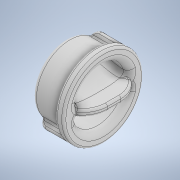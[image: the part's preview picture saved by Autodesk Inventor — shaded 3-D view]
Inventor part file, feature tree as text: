
AUTODESK INVENTOR PART (.ipt)
format: ipt  version: 2020 (Build 240168000, 168)  size: 1,119,744 bytes
history: native  units: in
note: dims shown in document units (in); Inventor stores cm internally (conversion verified against a paired STEP export)
features: fillet x10, extrude x5, sketch x5
ambient origin geometry x8: Origin, YZ Plane, XZ Plane, XY Plane, X Axis, Y Axis, Z Axis, Center Point
bodies: Solid1 (feature_tree)
feature tree (20):
  extrude  "Extrusion1"  Depth=0.5512in TaperAngle=0.0deg
  extrude  "Extrusion2"  TaperAngle=45.0deg  [1 undecoded]
  extrude  "Extrusion3"  Depth=0.0984in
  extrude  "Extrusion4"  Depth=0.4724in TaperAngle=0.0deg
  extrude  "Extrusion5"  Depth=0.1575in TaperAngle=0.0deg
  fillet  "Fillet1"  Radius=1.0236in
  fillet  "Fillet2"  Radius=0.5906in
  fillet  "Fillet3"  Radius=0.0591in
  fillet  "Fillet4"  Radius=0.0591in
  fillet  "Fillet5"  Radius=0.7874in
  fillet  "Fillet6"  Radius=0.5118in
  fillet  "Fillet7"  Radius=0.0787in
  fillet  "Fillet8"  Radius=0.4724in
  fillet  "Fillet9"  Radius=0.1181in
  fillet  "Fillet10"  Radius=0.0394in
  sketch  "Sketch1"  dims[d0=1.2598in d1=0.5512in d2=0.0in]
  sketch  "Sketch2"  dims[d3=1.4961in d4=45.0deg]
  sketch  "Sketch3"  dims[d5=0.0394in d6=0.0984in]
  sketch  "Sketch4"  dims[d7=0.1969in d8=0.4724in d9=0.0in]
  sketch  "Sketch5"  dims[d10=1.4961in d11=0.1575in d12=0.0in d13=1.0236in d14=0.5906in d15=0.0in d16=0.0591in d17=0.0591in d18=0.7874in d19=0.0in d20=0.5118in d21=0.0787in d22=0.4724in d23=0.1181in d24=0.0394in d25=0.0394in d26=0.0394in d27=0.0787in d28=0.1181in d29=0.0394in]
note: 1 required parameter value undecoded (feature->parameter linkage not recoverable at this tier; creation-order binding heuristic only, values carry confidence <= 0.55)
